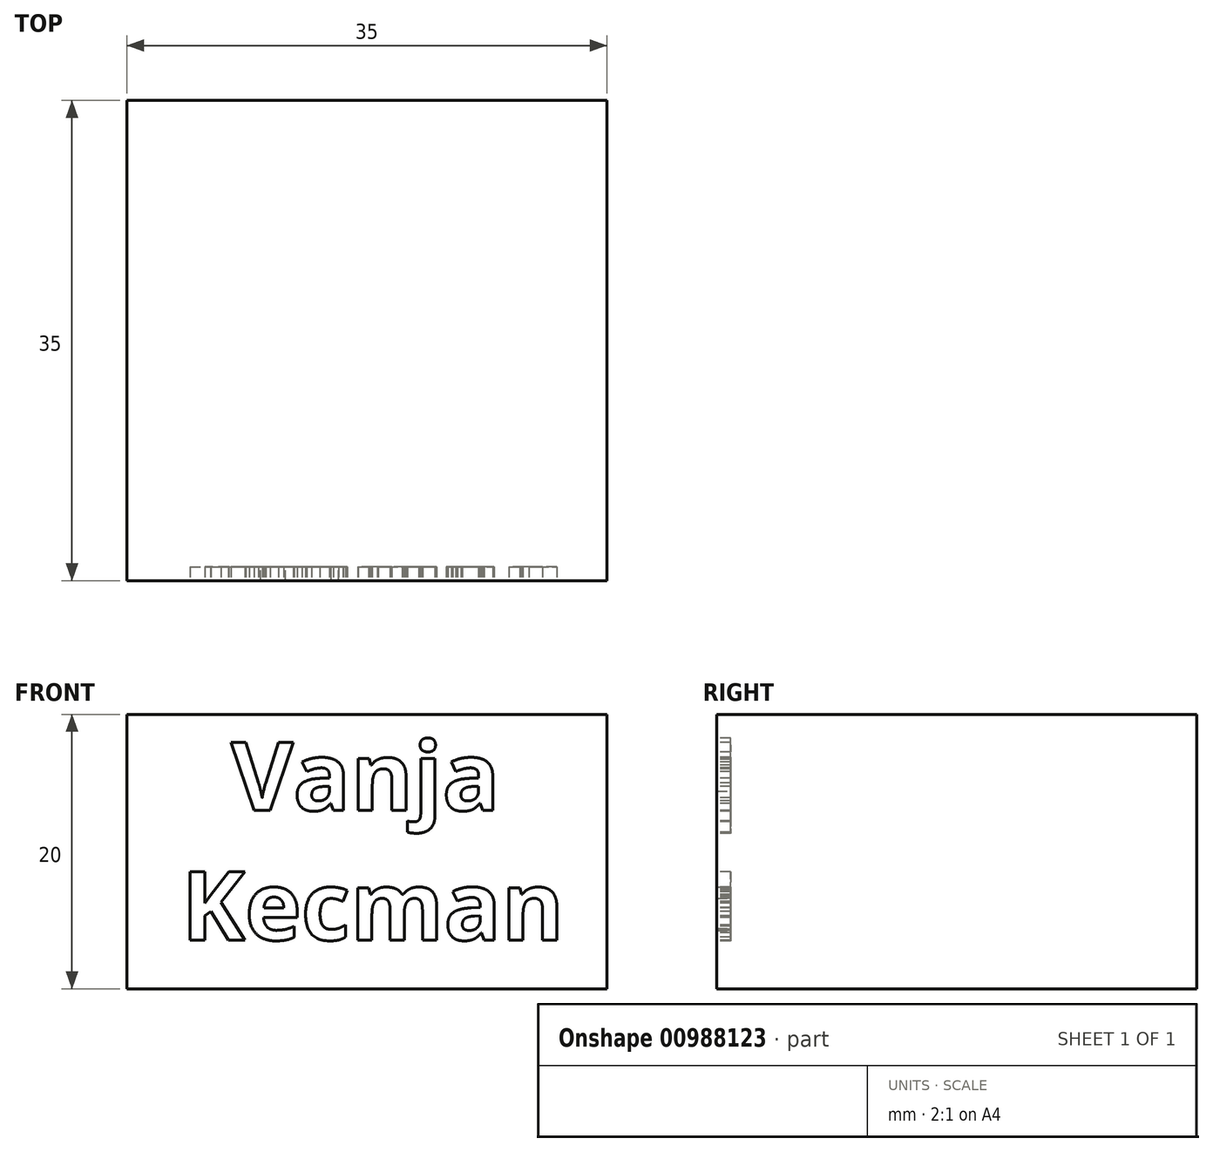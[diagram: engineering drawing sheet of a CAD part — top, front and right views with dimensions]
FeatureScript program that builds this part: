
annotation { "Feature Type Name" : "Feature", "Feature Type Description" : "" }
export const myFeature = defineFeature(function(context is Context, id is Id, definition is map)
    precondition{}
    {
        {
            var Q0;
            Q0=qCreatedBy(makeId("Top.planeOp"),FACE);
            var sketch = newSketch(context, id + "F0", { "sketchPlane" : qUnion([Q0])});
            skLineSegment(sketch, "E0.bottom", {"start": v(0, 0) * mm, "end": v(35, 0) * mm});
            skLineSegment(sketch, "E0.top", {"start": v(0, 35) * mm, "end": v(35, 35) * mm});
            skLineSegment(sketch, "E0.left", {"start": v(0, 0) * mm, "end": v(0, 35) * mm});
            skLineSegment(sketch, "E0.right", {"start": v(35, 0) * mm, "end": v(35, 35) * mm});
            skSolve(sketch);
        }
        {
            var Q0;
            Q0 = qSketchRegion(id + "F0", true);
            extrude(context, id + "F1", {"entities" : qUnion([Q0]), "depth" : 20 * mm, "offsetDistance" : 25 * mm});
        }
        {
            var Q0;
            Q0=makeQuery(id+"F1.opExtrude","SWEPT_FACE",FACE,{"disambiguationData":[OSD([sQuery(id+"F0.wireOp",EDGE,"E0.bottom")])]});
            var sketch = newSketch(context, id + "F2", { "sketchPlane" : qUnion([Q0])});
            skText(sketch, "E1", { "text": "  Vanja\nKecman", "fontName": "OpenSans-Bold.ttf"});
            const initialGuessF2  = {"E1": [0.004, 0.013, 1, 0, 0.005]};
            skSetInitialGuess(sketch, initialGuessF2);
            skSolve(sketch);
        }
        {
            var Q0;
            Q0 = qSketchRegion(id + "F2", true);
            extrude(context, id + "F3", {"entities" : qUnion([Q0]), "operationType" : NewBodyOperationType.REMOVE, "oppositeDirection" : true, "depth" : 1 * mm, "offsetDistance" : 25 * mm});
        }
    });
